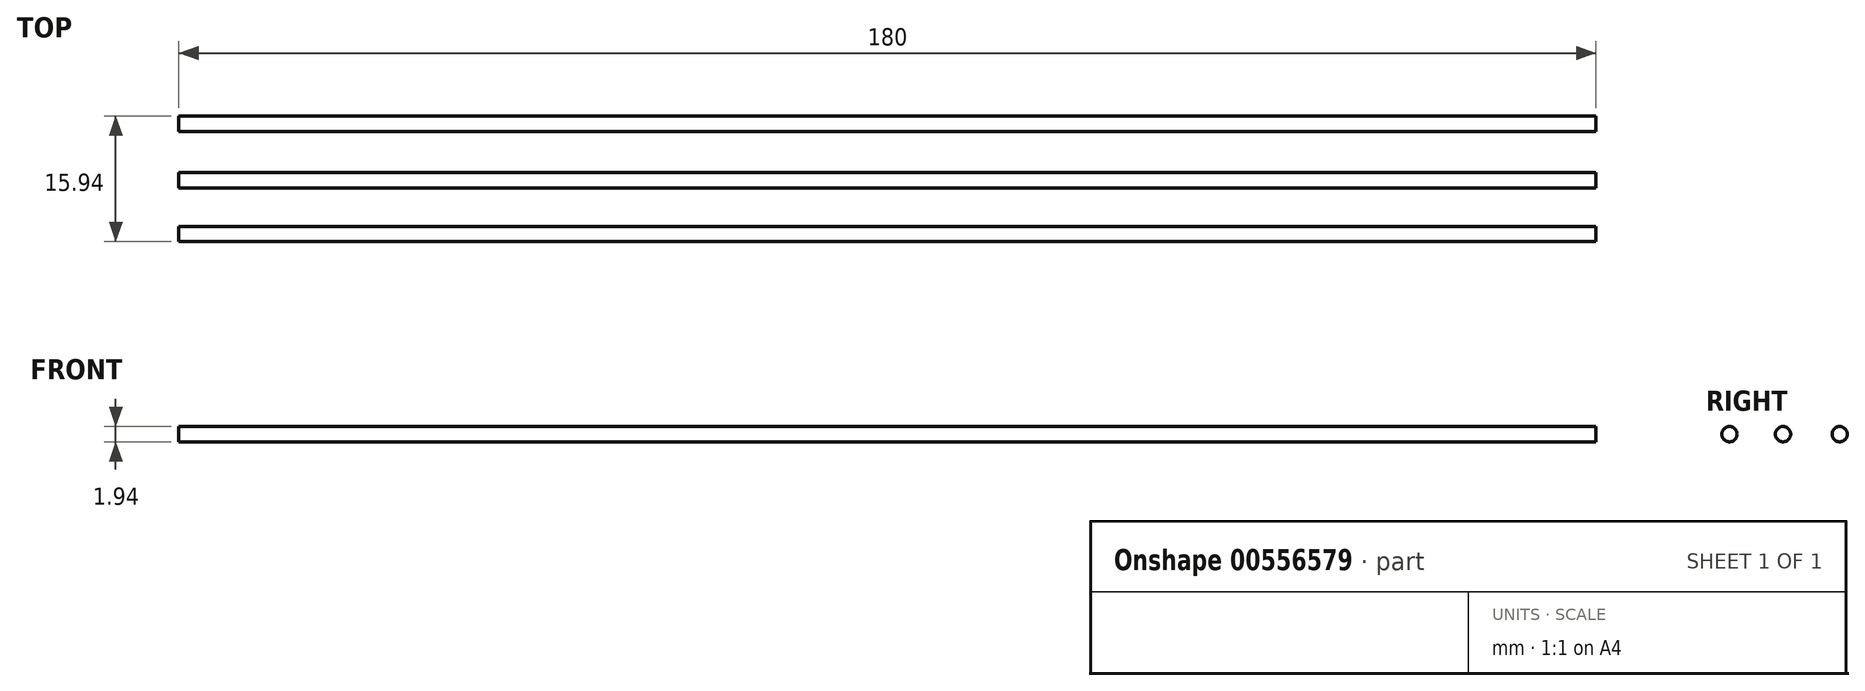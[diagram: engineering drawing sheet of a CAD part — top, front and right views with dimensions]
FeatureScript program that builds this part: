
annotation { "Feature Type Name" : "Feature", "Feature Type Description" : "" }
export const myFeature = defineFeature(function(context is Context, id is Id, definition is map)
    precondition{}
    {
        {
            var Q0;
            Q0=qCreatedBy(makeId("Right.planeOp"),FACE);
            var sketch = newSketch(context, id + "F0", { "sketchPlane" : qUnion([Q0])});
            skCircle(sketch, "E0", {"center": v(0, 0) * mm, "radius": 0.97 * mm});
            skCircle(sketch, "E1.1.0.0", {"center": v(0, -3.6) * mm, "radius": 0.97 * mm});
            skCircle(sketch, "E1.2.0.0", {"center": v(0, -7.2) * mm, "radius": 0.97 * mm});
            skLineSegment(sketch, "E1.direction1", {"start": v(0, 0) * mm, "end": v(0, -3.6) * mm, "construction": true});
            skSolve(sketch);
        }
        {
            var Q0;
            Q0=sQuery(id+"F0.wireOp",EDGE,"E0");
            var Q1;
            Q1=sQuery(id+"F0.wireOp",EDGE,"E1.1.0.0");
            var Q2;
            Q2=sQuery(id+"F0.wireOp",EDGE,"E1.2.0.0");
            extrude(context, id + "F1", {"bodyType" : ExtendedToolBodyType.SURFACE, "surfaceEntities" : qUnion([Q0, Q1, Q2]), "depth" : 180 * mm, "offsetDistance" : 25 * mm});
        }
        {
            var Q0;
            Q0=makeQuery(id+"F1.opExtrude","SWEPT_BODY",BODY,{"disambiguationData":[OSD([sQuery(id+"F0.wireOp",EDGE,"E0")])]});
            var Q1;
            Q1=makeQuery(id+"F1.opExtrude","SWEPT_BODY",BODY,{"disambiguationData":[OSD([sQuery(id+"F0.wireOp",EDGE,"E1.1.0.0")])]});
            var Q2;
            Q2=makeQuery(id+"F1.opExtrude","SWEPT_BODY",BODY,{"disambiguationData":[OSD([sQuery(id+"F0.wireOp",EDGE,"E1.2.0.0")])]});
            var Q3;
            Q3=makeQuery(id+"F1.opExtrude","SWEPT_FACE",FACE,{"disambiguationData":[OSD([sQuery(id+"F0.wireOp",EDGE,"E0")])]});
            transform(context, id + "F2", {"entities" : qUnion([Q0, Q1, Q2]), "transformType" : TransformType.ROTATION, "transformAxis" : qUnion([Q3]), "angle" : 90 * degree, "oppositeDirection" : true, "makeCopy" : false});
        }
        {
            var Q0;
            Q0=makeQuery(id+"F1.opExtrude","SWEPT_BODY",BODY,{"disambiguationData":[OSD([sQuery(id+"F0.wireOp",EDGE,"E1.1.0.0")])]});
            transform(context, id + "F3", {"entities" : qUnion([Q0]), "transformType" : TransformType.TRANSLATION_3D, "dx" : 0 * mm, "dy" : -10.4 * mm, "dz" : 0 * mm, "makeCopy" : false});
        }
    });
